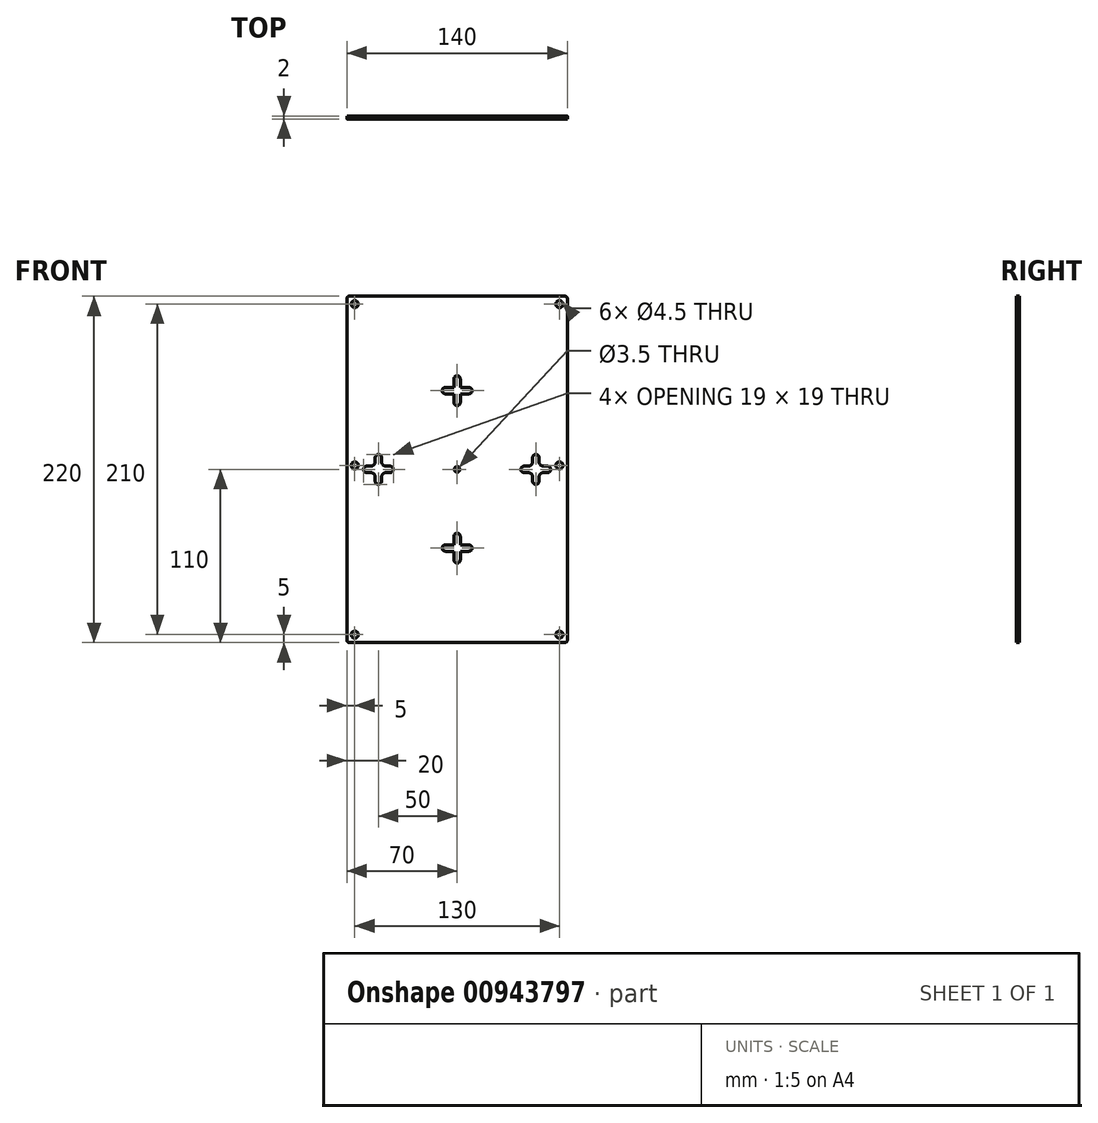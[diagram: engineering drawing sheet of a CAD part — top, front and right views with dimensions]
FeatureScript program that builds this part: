
annotation { "Feature Type Name" : "Feature", "Feature Type Description" : "" }
export const myFeature = defineFeature(function(context is Context, id is Id, definition is map)
    precondition{}
    {
        {
            var Q0;
            Q0=qCreatedBy(makeId("Front.planeOp"),FACE);
            var sketch = newSketch(context, id + "F0", { "sketchPlane" : qUnion([Q0])});
            skLineSegment(sketch, "E0.bottom", {"start": v(0, 0) * mm, "end": v(140, 0) * mm});
            skLineSegment(sketch, "E0.top", {"start": v(0, 220) * mm, "end": v(140, 220) * mm});
            skLineSegment(sketch, "E0.left", {"start": v(0, 0) * mm, "end": v(0, 220) * mm});
            skLineSegment(sketch, "E0.right", {"start": v(140, 0) * mm, "end": v(140, 220) * mm});
            skCircle(sketch, "E1", {"center": v(5, 215) * mm, "radius": 2.25 * mm});
            skCircle(sketch, "E2", {"center": v(5, 112.5) * mm, "radius": 2.25 * mm});
            skCircle(sketch, "E3", {"center": v(5, 5) * mm, "radius": 2.25 * mm});
            skCircle(sketch, "E4", {"center": v(135, 112.5) * mm, "radius": 2.25 * mm});
            skCircle(sketch, "E5", {"center": v(135, 215) * mm, "radius": 2.25 * mm});
            skCircle(sketch, "E6", {"center": v(135, 5) * mm, "radius": 2.25 * mm});
            skSolve(sketch);
        }
        {
            var Q0;
            Q0=makeQuery(id+"F0.imprint","IMPRINT",FACE,{"disambiguationData":[TD([[makeQuery(id+"F0.imprint","IMPRINT",EDGE,{"derivedFrom":sQuery(id+"F0.wireOp",EDGE,"E0.bottom")}),1.0]])]});
            extrude(context, id + "F1", {"entities" : qUnion([Q0]), "depth" : 2 * mm, "offsetDistance" : 25 * mm});
        }
        {
            var Q0;
            Q0=makeQuery(id+"F1.opExtrude","CAP_FACE",FACE,{"disambiguationData":[OSD([sQuery(id+"F0.wireOp",EDGE,"E0.bottom"),sQuery(id+"F0.wireOp",EDGE,"E0.top"),sQuery(id+"F0.wireOp",EDGE,"E0.left"),sQuery(id+"F0.wireOp",EDGE,"E0.right"),sQuery(id+"F0.wireOp",EDGE,"E1"),sQuery(id+"F0.wireOp",EDGE,"E2"),sQuery(id+"F0.wireOp",EDGE,"E3"),sQuery(id+"F0.wireOp",EDGE,"E4"),sQuery(id+"F0.wireOp",EDGE,"E5"),sQuery(id+"F0.wireOp",EDGE,"E6")])],"isStart":false});
            var sketch = newSketch(context, id + "F2", { "sketchPlane" : qUnion([Q0])});
            skLineSegment(sketch, "E7", {"start": v(20, 117.5) * mm, "end": v(20, 102.5) * mm});
            skPoint(sketch, "E8.endSnap0", {"position": v(20, 110) * mm});
            skLineSegment(sketch, "E9", {"start": v(12.5, 110) * mm, "end": v(27.5, 110) * mm});
            skArc(sketch, "E10.0.startCap", {"start": v(12.5, 108) * mm, "mid": v(10.5, 110) * mm, "end": v(12.5, 112) * mm});
            skArc(sketch, "E10.0.endCap", {"start": v(27.5, 112) * mm, "mid": v(29.5, 110) * mm, "end": v(27.5, 108) * mm});
            skLineSegment(sketch, "E10.0.left", {"start": v(12.5, 112) * mm, "end": v(27.5, 112) * mm});
            skLineSegment(sketch, "E10.0.right", {"start": v(12.5, 108) * mm, "end": v(27.5, 108) * mm});
            skArc(sketch, "E10.1.startCap", {"start": v(18, 117.5) * mm, "mid": v(20, 119.5) * mm, "end": v(22, 117.5) * mm});
            skArc(sketch, "E10.1.endCap", {"start": v(22, 102.5) * mm, "mid": v(20, 100.5) * mm, "end": v(18, 102.5) * mm});
            skLineSegment(sketch, "E10.1.left", {"start": v(22, 117.5) * mm, "end": v(22, 102.5) * mm});
            skLineSegment(sketch, "E10.1.right", {"start": v(18, 117.5) * mm, "end": v(18, 102.5) * mm});
            skPoint(sketch, "E11.1.0.0", {"position": v(120, 110) * mm});
            skLineSegment(sketch, "E11.1.0.1", {"start": v(120, 117.5) * mm, "end": v(120, 102.5) * mm});
            skLineSegment(sketch, "E11.1.0.2", {"start": v(118, 117.5) * mm, "end": v(118, 102.5) * mm});
            skLineSegment(sketch, "E11.1.0.3", {"start": v(122, 117.5) * mm, "end": v(122, 102.5) * mm});
            skArc(sketch, "E11.1.0.4", {"start": v(112.5, 108) * mm, "mid": v(110.5, 110) * mm, "end": v(112.5, 112) * mm});
            skLineSegment(sketch, "E11.1.0.5", {"start": v(112.5, 108) * mm, "end": v(127.5, 108) * mm});
            skArc(sketch, "E11.1.0.6", {"start": v(127.5, 112) * mm, "mid": v(129.5, 110) * mm, "end": v(127.5, 108) * mm});
            skLineSegment(sketch, "E11.1.0.7", {"start": v(112.5, 112) * mm, "end": v(127.5, 112) * mm});
            skArc(sketch, "E11.1.0.8", {"start": v(122, 102.5) * mm, "mid": v(120, 100.5) * mm, "end": v(118, 102.5) * mm});
            skLineSegment(sketch, "E11.1.0.9", {"start": v(112.5, 110) * mm, "end": v(127.5, 110) * mm});
            skArc(sketch, "E11.1.0.10", {"start": v(118, 117.5) * mm, "mid": v(120, 119.5) * mm, "end": v(122, 117.5) * mm});
            skLineSegment(sketch, "E11.direction1", {"start": v(18, 102.5) * mm, "end": v(118, 102.5) * mm, "construction": true});
            skCircle(sketch, "E12", {"center": v(70, 110) * mm, "radius": 1.75 * mm});
            skLineSegment(sketch, "E13", {"start": v(70, 167.5) * mm, "end": v(70, 152.5) * mm});
            skLineSegment(sketch, "E14", {"start": v(77.5, 160) * mm, "end": v(62.5, 160) * mm});
            skArc(sketch, "E15.0.startCap", {"start": v(68, 167.5) * mm, "mid": v(70, 169.5) * mm, "end": v(72, 167.5) * mm});
            skArc(sketch, "E15.0.endCap", {"start": v(72, 152.5) * mm, "mid": v(70, 150.5) * mm, "end": v(68, 152.5) * mm});
            skLineSegment(sketch, "E15.0.left", {"start": v(72, 167.5) * mm, "end": v(72, 152.5) * mm});
            skLineSegment(sketch, "E15.0.right", {"start": v(68, 167.5) * mm, "end": v(68, 152.5) * mm});
            skArc(sketch, "E15.1.startCap", {"start": v(77.5, 162) * mm, "mid": v(79.5, 160) * mm, "end": v(77.5, 158) * mm});
            skArc(sketch, "E15.1.endCap", {"start": v(62.5, 158) * mm, "mid": v(60.5, 160) * mm, "end": v(62.5, 162) * mm});
            skLineSegment(sketch, "E15.1.left", {"start": v(77.5, 158) * mm, "end": v(62.5, 158) * mm});
            skLineSegment(sketch, "E15.1.right", {"start": v(77.5, 162) * mm, "end": v(62.5, 162) * mm});
            skLineSegment(sketch, "E16.0.1.0", {"start": v(77.5, 62) * mm, "end": v(62.5, 62) * mm});
            skLineSegment(sketch, "E16.0.1.1", {"start": v(77.5, 58) * mm, "end": v(62.5, 58) * mm});
            skLineSegment(sketch, "E16.0.1.2", {"start": v(70, 67.5) * mm, "end": v(70, 52.5) * mm});
            skLineSegment(sketch, "E16.0.1.3", {"start": v(77.5, 60) * mm, "end": v(62.5, 60) * mm});
            skLineSegment(sketch, "E16.0.1.4", {"start": v(72, 67.5) * mm, "end": v(72, 52.5) * mm});
            skLineSegment(sketch, "E16.0.1.5", {"start": v(68, 67.5) * mm, "end": v(68, 52.5) * mm});
            skArc(sketch, "E16.0.1.6", {"start": v(77.5, 62) * mm, "mid": v(79.5, 60) * mm, "end": v(77.5, 58) * mm});
            skArc(sketch, "E16.0.1.7", {"start": v(68, 67.5) * mm, "mid": v(70, 69.5) * mm, "end": v(72, 67.5) * mm});
            skArc(sketch, "E16.0.1.8", {"start": v(62.5, 58) * mm, "mid": v(60.5, 60) * mm, "end": v(62.5, 62) * mm});
            skArc(sketch, "E16.0.1.9", {"start": v(72, 52.5) * mm, "mid": v(70, 50.5) * mm, "end": v(68, 52.5) * mm});
            skLineSegment(sketch, "E16.direction1", {"start": v(68, 152.5) * mm, "end": v(93, 152.5) * mm, "construction": true});
            skLineSegment(sketch, "E16.direction2", {"start": v(68, 152.5) * mm, "end": v(68, 52.5) * mm, "construction": true});
            skSolve(sketch);
        }
        {
            var Q0;
            Q0 = qSketchRegion(id + "F2", true);
            extrude(context, id + "F3", {"entities" : qUnion([Q0]), "operationType" : NewBodyOperationType.REMOVE, "oppositeDirection" : true, "depth" : 2 * mm, "offsetDistance" : 25 * mm});
        }
        {
            var Q0;
            Q0=makeQuery(id+"F3.boolean.opBoolean","COPY",EDGE,{"derivedFrom":makeQuery(id+"F3.opExtrude","SWEPT_EDGE",EDGE,{"disambiguationData":[OSD([sQuery(id+"F2.wireOp",EDGE,"E10.0.left"),sQuery(id+"F2.wireOp",EDGE,"E10.1.right")])]})});
            var Q1;
            Q1=makeQuery(id+"F3.boolean.opBoolean","COPY",EDGE,{"derivedFrom":makeQuery(id+"F3.opExtrude","SWEPT_EDGE",EDGE,{"disambiguationData":[OSD([sQuery(id+"F2.wireOp",EDGE,"E10.0.left"),sQuery(id+"F2.wireOp",EDGE,"E10.1.left")])]})});
            var Q2;
            Q2=makeQuery(id+"F3.boolean.opBoolean","COPY",EDGE,{"derivedFrom":makeQuery(id+"F3.opExtrude","SWEPT_EDGE",EDGE,{"disambiguationData":[OSD([sQuery(id+"F2.wireOp",EDGE,"E10.0.right"),sQuery(id+"F2.wireOp",EDGE,"E10.1.right")])]})});
            var Q3;
            Q3=makeQuery(id+"F3.boolean.opBoolean","COPY",EDGE,{"derivedFrom":makeQuery(id+"F3.opExtrude","SWEPT_EDGE",EDGE,{"disambiguationData":[OSD([sQuery(id+"F2.wireOp",EDGE,"E10.0.right"),sQuery(id+"F2.wireOp",EDGE,"E10.1.left")])]})});
            var Q4;
            Q4=makeQuery(id+"F3.boolean.opBoolean","COPY",EDGE,{"derivedFrom":makeQuery(id+"F3.opExtrude","SWEPT_EDGE",EDGE,{"disambiguationData":[OSD([sQuery(id+"F2.wireOp",EDGE,"E11.1.0.2"),sQuery(id+"F2.wireOp",EDGE,"E11.1.0.7")])]})});
            var Q5;
            Q5=makeQuery(id+"F3.boolean.opBoolean","COPY",EDGE,{"derivedFrom":makeQuery(id+"F3.opExtrude","SWEPT_EDGE",EDGE,{"disambiguationData":[OSD([sQuery(id+"F2.wireOp",EDGE,"E11.1.0.3"),sQuery(id+"F2.wireOp",EDGE,"E11.1.0.7")])]})});
            var Q6;
            Q6=makeQuery(id+"F3.boolean.opBoolean","COPY",EDGE,{"derivedFrom":makeQuery(id+"F3.opExtrude","SWEPT_EDGE",EDGE,{"disambiguationData":[OSD([sQuery(id+"F2.wireOp",EDGE,"E11.1.0.2"),sQuery(id+"F2.wireOp",EDGE,"E11.1.0.5")])]})});
            var Q7;
            Q7=makeQuery(id+"F3.boolean.opBoolean","COPY",EDGE,{"derivedFrom":makeQuery(id+"F3.opExtrude","SWEPT_EDGE",EDGE,{"disambiguationData":[OSD([sQuery(id+"F2.wireOp",EDGE,"E11.1.0.3"),sQuery(id+"F2.wireOp",EDGE,"E11.1.0.5")])]})});
            fillet(context, id + "F4", {"entities" : qUnion([Q0, Q1, Q2, Q3, Q4, Q5, Q6, Q7]), "radius" : 3 * mm, "tangentPropagation" : true, "allowEdgeOverflow" : false});
        }
        {
            var Q0;
            Q0=makeQuery(id+"F1.opExtrude","SWEPT_EDGE",EDGE,{"disambiguationData":[OSD([sQuery(id+"F0.wireOp",EDGE,"E0.top"),sQuery(id+"F0.wireOp",EDGE,"E0.left")])]});
            var Q1;
            Q1=makeQuery(id+"F1.opExtrude","SWEPT_EDGE",EDGE,{"disambiguationData":[OSD([sQuery(id+"F0.wireOp",EDGE,"E0.top"),sQuery(id+"F0.wireOp",EDGE,"E0.right")])]});
            var Q2;
            Q2=makeQuery(id+"F1.opExtrude","SWEPT_EDGE",EDGE,{"disambiguationData":[OSD([sQuery(id+"F0.wireOp",EDGE,"E0.bottom"),sQuery(id+"F0.wireOp",EDGE,"E0.left")])]});
            var Q3;
            Q3=makeQuery(id+"F1.opExtrude","SWEPT_EDGE",EDGE,{"disambiguationData":[OSD([sQuery(id+"F0.wireOp",EDGE,"E0.bottom"),sQuery(id+"F0.wireOp",EDGE,"E0.right")])]});
            fillet(context, id + "F5", {"entities" : qUnion([Q0, Q1, Q2, Q3]), "radius" : 1.5 * mm, "tangentPropagation" : true, "allowEdgeOverflow" : false});
        }
    });
